# Revit family: Rail_Guardrail-Base_FIXFAST_GW32-KATTSAFE
name_source: partatom
category: Generic Models
units: mm (PartAtom-declared; Revit-internal decimal feet)

## family parameters
Always vertical = No
Can host rebar = No
Classification Number = 23.30.80.11
Cut with Voids When Loaded = No
Maintain Annotation Orientation = No
Part Type = Normal
Room Calculation Point = No
Round Connector Dimension = Use Diameter
Shared = No
Work Plane-Based = Yes

## types (1)
- as Specified
    Assembly Code = E1090900
    Capacity = as Specified
    Construction Details = http://www.arcat.com
    Default Elevation = 0' - 0"
    Description = FIXFAST KATTSAFE GW32 Guardrail System
    Expected Lifespan (Years) = 0
    Green Building-LEED = http://www.arcat.com
    Keynote = 05 52 00
    Maintenance Schedule (Months) = 0
    Manufacturer = FIXFAST USA
    Manufacturer Fax = 317-769-5560
    Manufacturer Website = http://www.fixfastusa.com
    Model = GW32 Base
    Product Data = http://www.arcat.com
    Revision = R1_2017-06
    Sales Information = http://www.fixfastusa.com
    Specification = http://www.arcat.com
    Standards Conformance = OSHA 29 CFR 1910.29
    URL = http://www.fixfastusa.com
    Unit Width = 0' - 2 3/4"
    Warranty Duration (Years) = 0

## geometry (parser evidence)
native form markers: Sweep x2
no freeform markers — native parametric forms only
